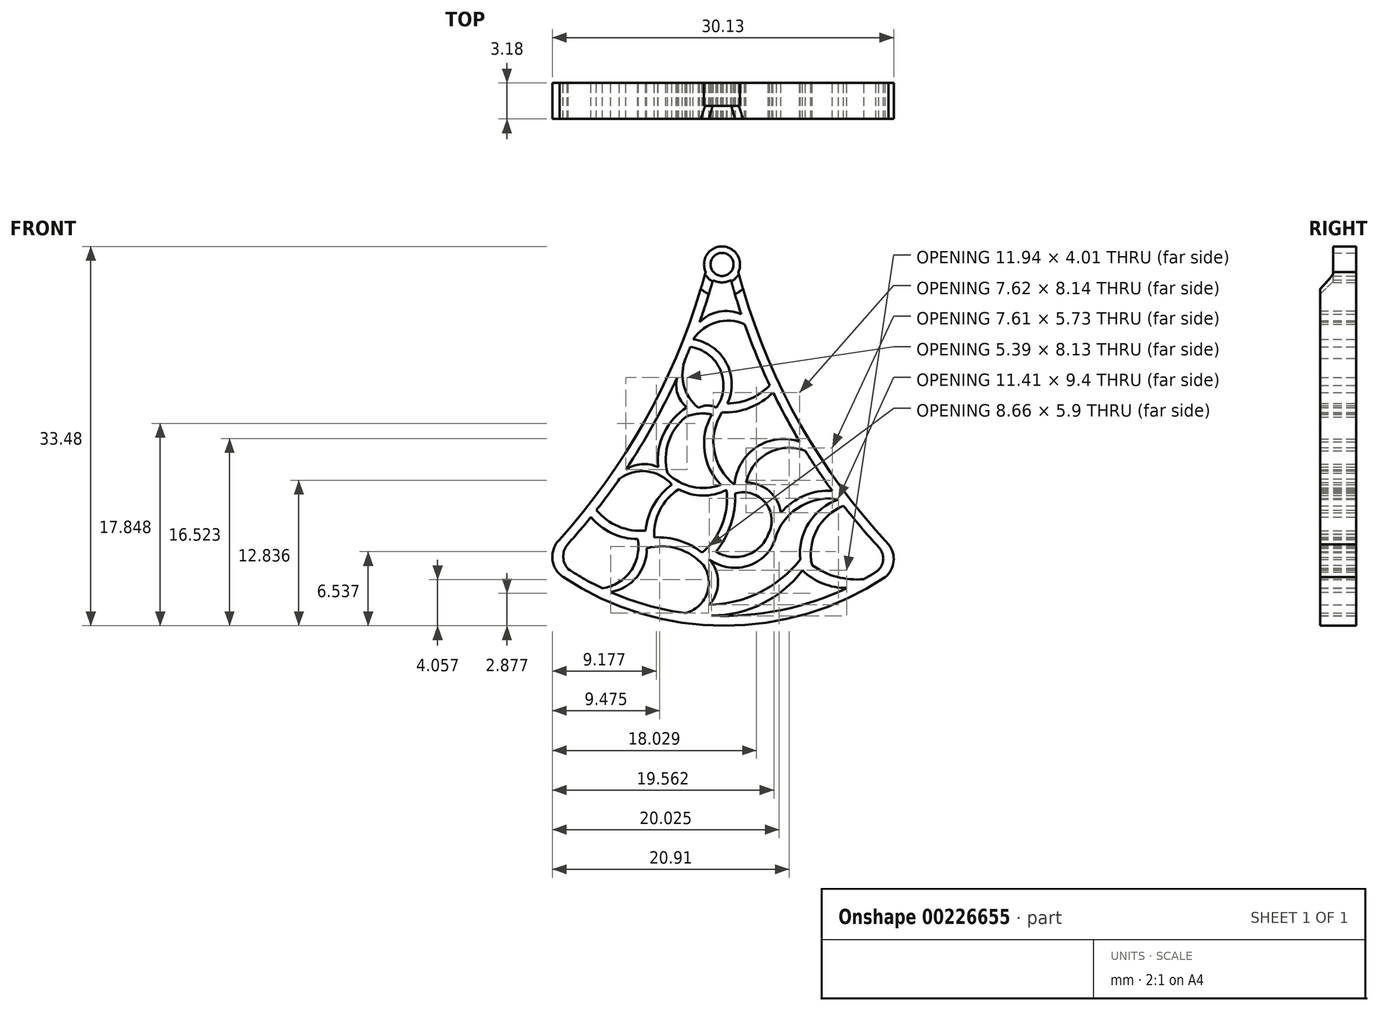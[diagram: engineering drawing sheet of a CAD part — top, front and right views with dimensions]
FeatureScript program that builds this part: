
annotation { "Feature Type Name" : "Feature", "Feature Type Description" : "" }
export const myFeature = defineFeature(function(context is Context, id is Id, definition is map)
    precondition{}
    {
        {
            var Q0;
            Q0=qCreatedBy(makeId("Front.planeOp"),FACE);
            var sketch = newSketch(context, id + "F0", { "sketchPlane" : qUnion([Q0])});
            skLineSegment(sketch, "E0", {"start": v(0, 0) * mm, "end": v(0, -5) * mm});
            skArc(sketch, "E1", {"start": v(-14.05, -27.57) * mm, "mid": v(0.17, -31.9) * mm, "end": v(14.4, -27.6) * mm});
            skArc(sketch, "E2", {"start": v(-14.34, -24.3) * mm, "mid": v(-6.5, -13.24) * mm, "end": v(-1.44, -0.66) * mm});
            skArc(sketch, "E3", {"start": v(1.44, -0.67) * mm, "mid": v(6.57, -13.51) * mm, "end": v(14.7, -24.7) * mm});
            skArc(sketch, "E4.0", {"start": v(-13.67, -24.77) * mm, "mid": v(-12.6, -23.54) * mm, "end": v(-11.56, -22.29) * mm});
            skArc(sketch, "E5", {"start": v(-13.58, -26.89) * mm, "mid": v(-12.1, -27.8) * mm, "end": v(-10.55, -28.6) * mm});
            skArc(sketch, "E6.trimOffspring", {"start": v(0.79, -1.38) * mm, "mid": v(1.22, -2.89) * mm, "end": v(1.7, -4.38) * mm});
            skArc(sketch, "E7", {"start": v(-11.56, -22.29) * mm, "mid": v(-9.72, -23.73) * mm, "end": v(-7.43, -24.24) * mm});
            skArc(sketch, "E8", {"start": v(-4.42, -19.44) * mm, "mid": v(-6.02, -21.21) * mm, "end": v(-6.74, -23.5) * mm});
            skArc(sketch, "E9", {"start": v(-9.84, -28.92) * mm, "mid": v(-7.52, -27.58) * mm, "end": v(-6.65, -25.06) * mm});
            skArc(sketch, "E10", {"start": v(-3.81, -19.84) * mm, "mid": v(-1.72, -20.4) * mm, "end": v(0.4, -19.9) * mm});
            skArc(sketch, "E11", {"start": v(-3.2, -13.47) * mm, "mid": v(-4.73, -15.71) * mm, "end": v(-4.8, -18.43) * mm});
            skArc(sketch, "E12", {"start": v(-1.76, -25.44) * mm, "mid": v(-3.74, -24.38) * mm, "end": v(-5.97, -24.1) * mm});
            skArc(sketch, "E13", {"start": v(-3.96, -9.98) * mm, "mid": v(-3.92, -11.42) * mm, "end": v(-3.1, -12.61) * mm});
            skArc(sketch, "E14", {"start": v(-4.42, -19.44) * mm, "mid": v(-6.63, -18.27) * mm, "end": v(-9.05, -18.92) * mm});
            skArc(sketch, "E15", {"start": v(-1.12, -30.05) * mm, "mid": v(-0.35, -28.04) * mm, "end": v(-1.12, -26.03) * mm});
            skArc(sketch, "E16", {"start": v(-0.52, -25.35) * mm, "mid": v(0.78, -22.93) * mm, "end": v(1.17, -20.2) * mm});
            skArc(sketch, "E17", {"start": v(-1.12, -26.03) * mm, "mid": v(2.46, -26.55) * mm, "end": v(4.82, -23.82) * mm});
            skArc(sketch, "E18", {"start": v(4.82, -23.82) * mm, "mid": v(4.94, -23.58) * mm, "end": v(5.04, -23.32) * mm});
            skArc(sketch, "E19", {"start": v(0, -13.06) * mm, "mid": v(-0.69, -16.46) * mm, "end": v(1.11, -19.44) * mm});
            skArc(sketch, "E20", {"start": v(-0.92, -31) * mm, "mid": v(3.55, -29.95) * mm, "end": v(7.1, -27) * mm});
            skArc(sketch, "E21", {"start": v(10.29, -20.73) * mm, "mid": v(7.67, -22.8) * mm, "end": v(6.9, -26.06) * mm});
            skArc(sketch, "E22", {"start": v(7.1, -27) * mm, "mid": v(8.9, -28.17) * mm, "end": v(11.02, -28.57) * mm});
            skArc(sketch, "E23", {"start": v(10.29, -20.73) * mm, "mid": v(7, -21.3) * mm, "end": v(4.82, -23.82) * mm});
            skArc(sketch, "E24", {"start": v(0.48, -12.28) * mm, "mid": v(0.38, -8.7) * mm, "end": v(-2.54, -6.6) * mm});
            skArc(sketch, "E25", {"start": v(-0.5, -12.65) * mm, "mid": v(-1.3, -12.45) * mm, "end": v(-2.08, -12.66) * mm});
            skArc(sketch, "E26", {"start": v(6.86, -15.64) * mm, "mid": v(3.05, -16.12) * mm, "end": v(1.11, -19.44) * mm});
            skArc(sketch, "E27", {"start": v(0, -13.06) * mm, "mid": v(2.44, -12.65) * mm, "end": v(4.5, -11.3) * mm});
            skArc(sketch, "E28", {"start": v(2, -5.27) * mm, "mid": v(-0.51, -5.11) * mm, "end": v(-2.54, -6.6) * mm});
            skArc(sketch, "E29", {"start": v(-10.55, -28.6) * mm, "mid": v(-8.07, -27.08) * mm, "end": v(-7.43, -24.24) * mm});
            skArc(sketch, "E30", {"start": v(-11.09, -21.68) * mm, "mid": v(-9.14, -23.13) * mm, "end": v(-6.74, -23.5) * mm});
            skArc(sketch, "E31", {"start": v(-3.81, -19.84) * mm, "mid": v(-5.48, -21.67) * mm, "end": v(-5.97, -24.1) * mm});
            skArc(sketch, "E32", {"start": v(-1.63, -26.57) * mm, "mid": v(-3.92, -25.1) * mm, "end": v(-6.65, -25.06) * mm});
            skArc(sketch, "E33", {"start": v(-3.24, -30.78) * mm, "mid": v(-1.34, -29.1) * mm, "end": v(-1.63, -26.57) * mm});
            skLineSegment(sketch, "E34.trimOffspring", {"start": v(0, -26.6) * mm, "end": v(0, -30.48) * mm});
            skArc(sketch, "E35", {"start": v(-5.64, -17.88) * mm, "mid": v(-7.1, -17.63) * mm, "end": v(-8.5, -18.1) * mm});
            skArc(sketch, "E36.trimOffspring", {"start": v(-11.09, -21.68) * mm, "mid": v(-10.05, -20.31) * mm, "end": v(-9.05, -18.92) * mm});
            skArc(sketch, "E37.trimOffspring", {"start": v(-9.84, -28.92) * mm, "mid": v(-6.6, -30.08) * mm, "end": v(-3.24, -30.78) * mm});
            skArc(sketch, "E38.trimOffspring", {"start": v(-2.4, -30.89) * mm, "mid": v(4.47, -30.65) * mm, "end": v(11.02, -28.57) * mm});
            skArc(sketch, "E39", {"start": v(-0.9, -13.26) * mm, "mid": v(-1.54, -16.48) * mm, "end": v(-0.11, -19.45) * mm});
            skArc(sketch, "E40", {"start": v(-3.1, -12.61) * mm, "mid": v(-5.12, -14.89) * mm, "end": v(-5.64, -17.88) * mm});
            skArc(sketch, "E41", {"start": v(-4.8, -18.43) * mm, "mid": v(-2.6, -19.63) * mm, "end": v(-0.11, -19.45) * mm});
            skArc(sketch, "E42", {"start": v(-1.76, -25.44) * mm, "mid": v(0.02, -22.95) * mm, "end": v(0.4, -19.9) * mm});
            skArc(sketch, "E43", {"start": v(7.35, -16.45) * mm, "mid": v(4.1, -16.64) * mm, "end": v(2.13, -19.25) * mm});
            skArc(sketch, "E44", {"start": v(-0.52, -25.35) * mm, "mid": v(2.16, -25.67) * mm, "end": v(4.1, -23.8) * mm});
            skArc(sketch, "E45", {"start": v(4.1, -23.8) * mm, "mid": v(3.82, -21.04) * mm, "end": v(1.17, -20.2) * mm});
            skArc(sketch, "E46", {"start": v(10.73, -21.3) * mm, "mid": v(8.37, -23.41) * mm, "end": v(7.95, -26.55) * mm});
            skPoint(sketch, "E46.endSnap0", {"position": v(2.46, -26.55) * mm});
            skArc(sketch, "E47", {"start": v(7.95, -26.55) * mm, "mid": v(10.13, -27.58) * mm, "end": v(12.53, -27.78) * mm});
            skArc(sketch, "E48", {"start": v(0.48, -12.28) * mm, "mid": v(2.5, -11.85) * mm, "end": v(4.2, -10.66) * mm});
            skArc(sketch, "E49", {"start": v(-0.5, -12.65) * mm, "mid": v(-0.15, -9.32) * mm, "end": v(-2.8, -7.27) * mm});
            skArc(sketch, "E50", {"start": v(-1.12, -30.05) * mm, "mid": v(3.34, -28.95) * mm, "end": v(6.9, -26.06) * mm});
            skArc(sketch, "E51", {"start": v(9.73, -19.98) * mm, "mid": v(7.23, -20.42) * mm, "end": v(5.19, -21.92) * mm});
            skArc(sketch, "E52", {"start": v(-3.22, -8.3) * mm, "mid": v(-3.37, -10.66) * mm, "end": v(-2.08, -12.66) * mm});
            skArc(sketch, "E53", {"start": v(1.7, -4.38) * mm, "mid": v(-0.25, -4.17) * mm, "end": v(-1.98, -5.1) * mm});
            skArc(sketch, "E54", {"start": v(-0.9, -13.26) * mm, "mid": v(-2.07, -13.17) * mm, "end": v(-3.2, -13.47) * mm});
            skArc(sketch, "E55.trimOffspring", {"start": v(5.19, -21.92) * mm, "mid": v(4.17, -20) * mm, "end": v(2.13, -19.25) * mm});
            skArc(sketch, "E56.trimOffspring", {"start": v(10.73, -21.3) * mm, "mid": v(12.24, -23.17) * mm, "end": v(13.83, -24.96) * mm});
            skArc(sketch, "E57.trimOffspring", {"start": v(12.53, -27.78) * mm, "mid": v(13.06, -27.47) * mm, "end": v(13.58, -27.15) * mm});
            skArc(sketch, "E58.trimOffspring", {"start": v(-8.5, -18.1) * mm, "mid": v(-6.07, -14.13) * mm, "end": v(-3.96, -9.98) * mm});
            skLineSegment(sketch, "E59.trimOffspring", {"start": v(0, -23) * mm, "end": v(0, -24.61) * mm});
            skArc(sketch, "E60.trimOffspring", {"start": v(-3.22, -8.3) * mm, "mid": v(-3, -7.78) * mm, "end": v(-2.8, -7.27) * mm});
            skArc(sketch, "E61.trimOffspring", {"start": v(-1.98, -5.1) * mm, "mid": v(-1.36, -3.24) * mm, "end": v(-0.8, -1.37) * mm});
            skArc(sketch, "E62.trimOffspring", {"start": v(2, -5.27) * mm, "mid": v(3.03, -8) * mm, "end": v(4.2, -10.66) * mm});
            skArc(sketch, "E63.trimOffspring", {"start": v(4.5, -11.3) * mm, "mid": v(5.64, -13.5) * mm, "end": v(6.86, -15.64) * mm});
            skArc(sketch, "E64.trimOffspring", {"start": v(7.35, -16.45) * mm, "mid": v(8.5, -18.24) * mm, "end": v(9.73, -19.98) * mm});
            skArc(sketch, "E65", {"start": v(-13.67, -24.77) * mm, "mid": v(-14, -25.84) * mm, "end": v(-13.58, -26.89) * mm});
            skArc(sketch, "E66", {"start": v(-14.34, -24.3) * mm, "mid": v(-14.97, -26) * mm, "end": v(-14.05, -27.57) * mm});
            skArc(sketch, "E67", {"start": v(13.58, -27.15) * mm, "mid": v(14.22, -26.12) * mm, "end": v(13.83, -24.96) * mm});
            skArc(sketch, "E68", {"start": v(14.02, -27.85) * mm, "mid": v(15.13, -26.3) * mm, "end": v(14.5, -24.49) * mm});
            skCircle(sketch, "E69", {"center": v(0, 0) * mm, "radius": 1.59 * mm});
            skCircle(sketch, "E70", {"center": v(0, 0) * mm, "radius": 1.02 * mm});
            skPoint(sketch, "E71.orphan", {"position": v(-1.27, 0) * mm});
            skPoint(sketch, "E72.orphan", {"position": v(1.27, 0) * mm});
            skSolve(sketch);
        }
        {
            var Q0;
            {var subQ28=sQuery(id+"F0.wireOp",EDGE,"E2");Q0=makeQuery(id+"F0.imprint","IMPRINT",FACE,{"disambiguationData":[TD([[makeQuery(id+"F0.imprint","IMPRINT",EDGE,{"derivedFrom":subQ28}),-1.0]])]});}
            extrude(context, id + "F3", {"entities" : qUnion([Q0]), "depth" : 3.17 * mm});
        }
        {
            var Q0;
            Q0=makeQuery(id+"F0.imprint","IMPRINT",FACE,{"disambiguationData":[TD([[makeQuery(id+"F0.imprint","IMPRINT",EDGE,{"derivedFrom":sQuery(id+"F0.wireOp",EDGE,"E70")}),-1.0]])]});
            extrude(context, id + "F1", {"entities" : qUnion([Q0]), "operationType" : NewBodyOperationType.ADD, "depth" : 2.03 * mm});
        }
        {
            var Q0;
            {var subQ0=sQuery(id+"F0.wireOp",EDGE,"E69");Q0=makeQuery(id+"F3.opExtrude","CAP_EDGE",EDGE,{"disambiguationData":[OSD([subQ0]),TDD([makeQuery(id+"F0.imprint","IMPRINT",EDGE,{"disambiguationData":[TD([[makeQuery(id+"F0.imprint","INTERSECT",VERTEX,{"derivedFrom":[sQuery(id+"F0.wireOp",EDGE,"E3"),subQ0]}),1.0]])],"derivedFrom":subQ0})])],"isStart":false});}
            var Q1;
            {var subQ0=sQuery(id+"F0.wireOp",EDGE,"E69");Q1=makeQuery(id+"F3.opExtrude","CAP_EDGE",EDGE,{"disambiguationData":[OSD([subQ0]),TDD([makeQuery(id+"F0.imprint","IMPRINT",EDGE,{"disambiguationData":[TD([[makeQuery(id+"F0.imprint","INTERSECT",VERTEX,{"derivedFrom":[sQuery(id+"F0.wireOp",EDGE,"E2"),subQ0]}),-1.0]])],"derivedFrom":subQ0})])],"isStart":false});}
            chamfer(context, id + "F2", {"entities" : qUnion([Q0, Q1]), "width" : 1.27 * mm, "tangentPropagation" : true});
        }
    });
